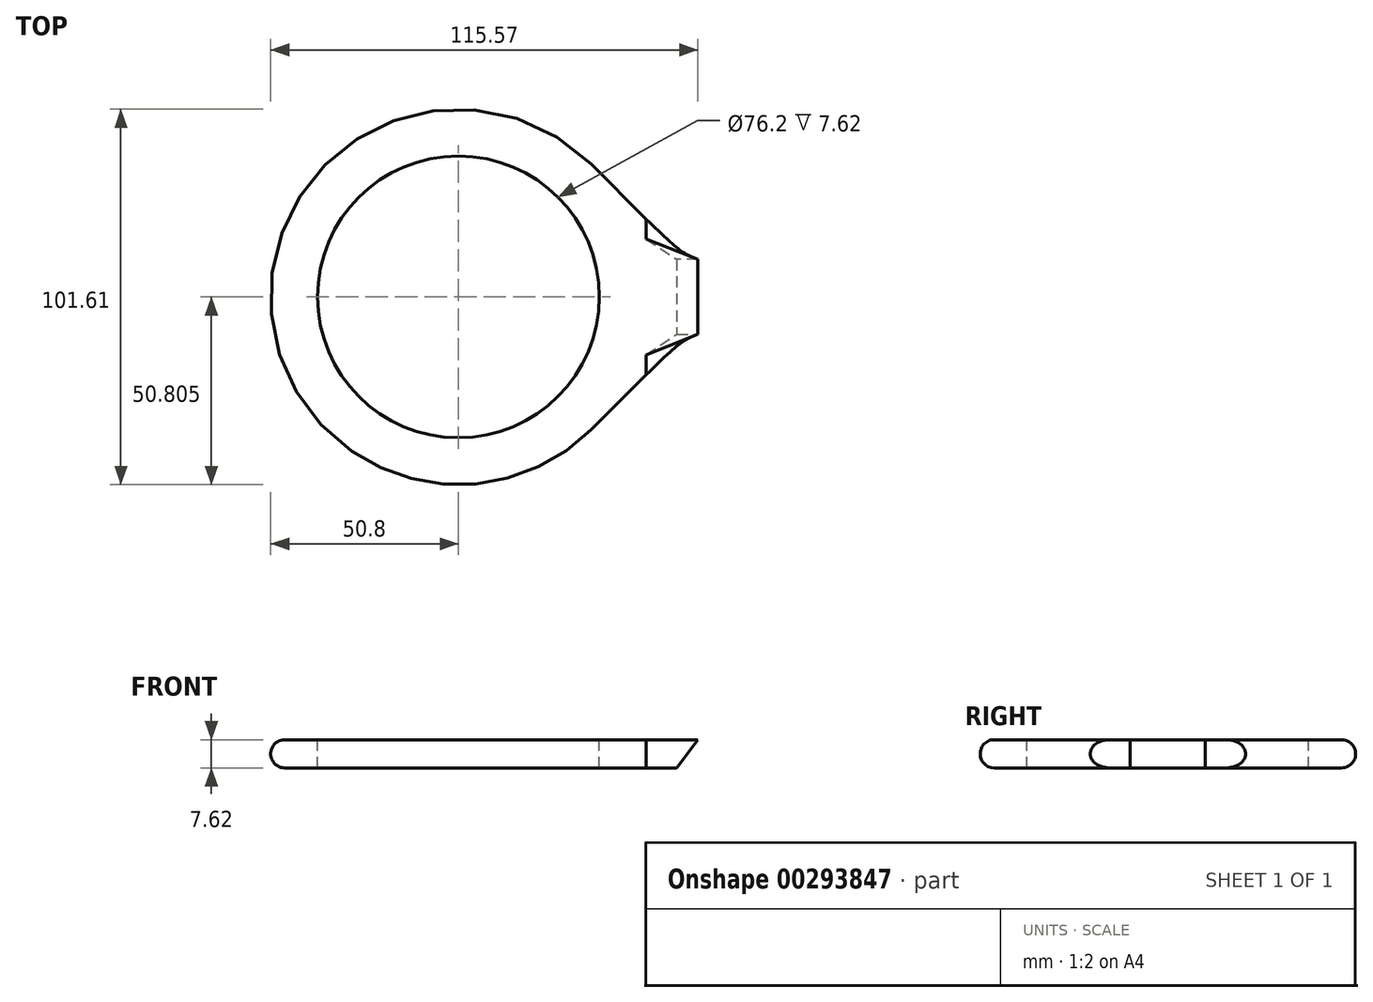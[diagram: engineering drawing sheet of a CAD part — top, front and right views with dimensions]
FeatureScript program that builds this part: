
annotation { "Feature Type Name" : "Feature", "Feature Type Description" : "" }
export const myFeature = defineFeature(function(context is Context, id is Id, definition is map)
    precondition{}
    {
        {
            var Q0;
            Q0=qCreatedBy(makeId("Top.planeOp"),FACE);
            var sketch = newSketch(context, id + "F0", { "sketchPlane" : qUnion([Q0])});
            skLineSegment(sketch, "E0.bottom", {"start": v(31.75, 24.77) * mm, "end": v(-31.75, 24.76) * mm});
            skLineSegment(sketch, "E0.top", {"start": v(31.75, 4.45) * mm, "end": v(-31.75, 4.44) * mm});
            skLineSegment(sketch, "E0.left", {"start": v(31.75, 24.77) * mm, "end": v(31.75, 4.45) * mm});
            skLineSegment(sketch, "E0.right", {"start": v(-31.75, 24.77) * mm, "end": v(-31.75, 4.44) * mm});
            skPoint(sketch, "E0.middle", {"position": v(0, 14.6) * mm});
            skLineSegment(sketch, "E1", {"start": v(-15.88, 24.76) * mm, "end": v(-15.88, 4.44) * mm});
            skLineSegment(sketch, "E2", {"start": v(15.88, 24.77) * mm, "end": v(15.88, 4.44) * mm});
            skCircle(sketch, "E3.cCircle", {"center": v(-82.55, 14.6) * mm, "radius": 50.8 * mm, "construction": true});
            skPoint(sketch, "E3.cCircle.centerSnap0", {"position": v(-31.75, 14.6) * mm});
            skLineSegment(sketch, "E3.0", {"start": v(-31.75, 35.65) * mm, "end": v(-31.75, -6.44) * mm});
            skLineSegment(sketch, "E3.1", {"start": v(-31.75, -6.44) * mm, "end": v(-61.5, -36.2) * mm});
            skLineSegment(sketch, "E3.2", {"start": v(-61.5, -36.2) * mm, "end": v(-103.6, -36.2) * mm});
            skLineSegment(sketch, "E3.3", {"start": v(-103.6, -36.2) * mm, "end": v(-133.35, -6.44) * mm});
            skLineSegment(sketch, "E3.4", {"start": v(-133.35, -6.44) * mm, "end": v(-133.35, 35.65) * mm});
            skLineSegment(sketch, "E3.5", {"start": v(-133.35, 35.65) * mm, "end": v(-103.6, 65.4) * mm});
            skLineSegment(sketch, "E3.6", {"start": v(-103.6, 65.4) * mm, "end": v(-61.5, 65.4) * mm});
            skLineSegment(sketch, "E3.7", {"start": v(-61.5, 65.4) * mm, "end": v(-31.75, 35.65) * mm});
            skPoint(sketch, "E3.0.midPoint", {"position": v(-31.75, 14.6) * mm});
            skCircle(sketch, "E4.cCircle", {"center": v(82.55, 14.6) * mm, "radius": 50.8 * mm, "construction": true});
            skPoint(sketch, "E4.cCircle.centerSnap0", {"position": v(31.75, 14.6) * mm});
            skLineSegment(sketch, "E4.0", {"start": v(31.75, -6.44) * mm, "end": v(31.75, 35.65) * mm});
            skLineSegment(sketch, "E4.1", {"start": v(31.75, 35.65) * mm, "end": v(61.5, 65.4) * mm});
            skLineSegment(sketch, "E4.2", {"start": v(61.5, 65.4) * mm, "end": v(103.6, 65.4) * mm});
            skLineSegment(sketch, "E4.3", {"start": v(103.6, 65.4) * mm, "end": v(133.35, 35.65) * mm});
            skLineSegment(sketch, "E4.4", {"start": v(133.35, 35.65) * mm, "end": v(133.35, -6.44) * mm});
            skLineSegment(sketch, "E4.5", {"start": v(133.35, -6.44) * mm, "end": v(103.6, -36.2) * mm});
            skLineSegment(sketch, "E4.6", {"start": v(103.6, -36.2) * mm, "end": v(61.5, -36.2) * mm});
            skLineSegment(sketch, "E4.7", {"start": v(61.5, -36.2) * mm, "end": v(31.75, -6.44) * mm});
            skPoint(sketch, "E4.0.midPoint", {"position": v(31.75, 14.6) * mm});
            skCircle(sketch, "E5.cCircle", {"center": v(-82.55, 14.6) * mm, "radius": 38.1 * mm, "construction": true});
            skLineSegment(sketch, "E5.0", {"start": v(-98.33, 52.7) * mm, "end": v(-66.77, 52.7) * mm});
            skLineSegment(sketch, "E5.1", {"start": v(-66.77, 52.7) * mm, "end": v(-44.45, 30.39) * mm});
            skLineSegment(sketch, "E5.2", {"start": v(-44.45, 30.39) * mm, "end": v(-44.45, -1.18) * mm});
            skLineSegment(sketch, "E5.3", {"start": v(-44.45, -1.18) * mm, "end": v(-66.77, -23.5) * mm});
            skLineSegment(sketch, "E5.4", {"start": v(-66.77, -23.5) * mm, "end": v(-98.33, -23.5) * mm});
            skLineSegment(sketch, "E5.5", {"start": v(-98.33, -23.5) * mm, "end": v(-120.65, -1.18) * mm});
            skLineSegment(sketch, "E5.6", {"start": v(-120.65, -1.18) * mm, "end": v(-120.65, 30.39) * mm});
            skLineSegment(sketch, "E5.7", {"start": v(-120.65, 30.39) * mm, "end": v(-98.33, 52.7) * mm});
            skPoint(sketch, "E5.0.midPoint", {"position": v(-82.55, 52.7) * mm});
            skCircle(sketch, "E6.cCircle", {"center": v(82.55, 14.6) * mm, "radius": 38.1 * mm, "construction": true});
            skLineSegment(sketch, "E6.0", {"start": v(66.77, 52.7) * mm, "end": v(98.33, 52.7) * mm});
            skLineSegment(sketch, "E6.1", {"start": v(98.33, 52.7) * mm, "end": v(120.65, 30.39) * mm});
            skLineSegment(sketch, "E6.2", {"start": v(120.65, 30.39) * mm, "end": v(120.65, -1.18) * mm});
            skLineSegment(sketch, "E6.3", {"start": v(120.65, -1.18) * mm, "end": v(98.33, -23.5) * mm});
            skLineSegment(sketch, "E6.4", {"start": v(98.33, -23.5) * mm, "end": v(66.77, -23.5) * mm});
            skLineSegment(sketch, "E6.5", {"start": v(66.77, -23.5) * mm, "end": v(44.45, -1.18) * mm});
            skLineSegment(sketch, "E6.6", {"start": v(44.45, -1.18) * mm, "end": v(44.45, 30.39) * mm});
            skLineSegment(sketch, "E6.7", {"start": v(44.45, 30.39) * mm, "end": v(66.77, 52.7) * mm});
            skPoint(sketch, "E6.0.midPoint", {"position": v(82.55, 52.7) * mm});
            skSolve(sketch);
        }
        {
            var Q0;
            {var subQ4=sQuery(id+"F0.wireOp",EDGE,"E3.1");Q0=makeQuery(id+"F0.imprint","IMPRINT",FACE,{"disambiguationData":[TD([[makeQuery(id+"F0.imprint","IMPRINT",EDGE,{"derivedFrom":subQ4}),-1.0]])]});}
            var Q1;
            {var subQ3=sQuery(id+"F0.wireOp",EDGE,"E1");Q1=makeQuery(id+"F0.imprint","IMPRINT",FACE,{"disambiguationData":[TD([[makeQuery(id+"F0.imprint","IMPRINT",EDGE,{"derivedFrom":subQ3}),-1.0]])]});}
            extrude(context, id + "F1", {"entities" : qUnion([Q0, Q1]), "depth" : 7.62 * mm});
        }
        {
            var Q0;
            Q0=makeQuery(id+"F1.opExtrude","CAP_EDGE",EDGE,{"disambiguationData":[OSD([sQuery(id+"F0.wireOp",EDGE,"E1")])],"isStart":true});
            chamfer(context, id + "F2", {"entities" : qUnion([Q0]), "chamferType" : ChamferType.TWO_OFFSETS, "width1" : 7.62 * mm, "oppositeDirection" : false, "width2" : 10.16 * mm, "tangentPropagation" : true});
        }
        {
            var Q0;
            Q0=makeQuery(id+"F1.opExtrude","SWEPT_EDGE",EDGE,{"disambiguationData":[OSD([sQuery(id+"F0.wireOp",EDGE,"E5.0"),sQuery(id+"F0.wireOp",EDGE,"E5.7")])]});
            var Q1;
            Q1=makeQuery(id+"F1.opExtrude","SWEPT_EDGE",EDGE,{"disambiguationData":[OSD([sQuery(id+"F0.wireOp",EDGE,"E5.0"),sQuery(id+"F0.wireOp",EDGE,"E5.1")])]});
            var Q2;
            Q2=makeQuery(id+"F1.opExtrude","SWEPT_EDGE",EDGE,{"disambiguationData":[OSD([sQuery(id+"F0.wireOp",EDGE,"E5.1"),sQuery(id+"F0.wireOp",EDGE,"E5.2")])]});
            var Q3;
            Q3=makeQuery(id+"F1.opExtrude","SWEPT_EDGE",EDGE,{"disambiguationData":[OSD([sQuery(id+"F0.wireOp",EDGE,"E5.2"),sQuery(id+"F0.wireOp",EDGE,"E5.3")])]});
            var Q4;
            Q4=makeQuery(id+"F1.opExtrude","SWEPT_EDGE",EDGE,{"disambiguationData":[OSD([sQuery(id+"F0.wireOp",EDGE,"E5.3"),sQuery(id+"F0.wireOp",EDGE,"E5.4")])]});
            var Q5;
            Q5=makeQuery(id+"F1.opExtrude","SWEPT_EDGE",EDGE,{"disambiguationData":[OSD([sQuery(id+"F0.wireOp",EDGE,"E5.4"),sQuery(id+"F0.wireOp",EDGE,"E5.5")])]});
            var Q6;
            Q6=makeQuery(id+"F1.opExtrude","SWEPT_EDGE",EDGE,{"disambiguationData":[OSD([sQuery(id+"F0.wireOp",EDGE,"E5.5"),sQuery(id+"F0.wireOp",EDGE,"E5.6")])]});
            var Q7;
            Q7=makeQuery(id+"F1.opExtrude","SWEPT_EDGE",EDGE,{"disambiguationData":[OSD([sQuery(id+"F0.wireOp",EDGE,"E5.6"),sQuery(id+"F0.wireOp",EDGE,"E5.7")])]});
            fillet(context, id + "F3", {"entities" : qUnion([Q0, Q1, Q2, Q3, Q4, Q5, Q6, Q7]), "radius" : 38.1 * mm, "tangentPropagation" : true, "allowEdgeOverflow" : false});
        }
        {
            var Q0;
            Q0=makeQuery(id+"F1.opExtrude","SWEPT_EDGE",EDGE,{"disambiguationData":[OSD([sQuery(id+"F0.wireOp",EDGE,"E3.1"),sQuery(id+"F0.wireOp",EDGE,"E3.2")])]});
            var Q1;
            Q1=makeQuery(id+"F1.opExtrude","SWEPT_EDGE",EDGE,{"disambiguationData":[OSD([sQuery(id+"F0.wireOp",EDGE,"E3.2"),sQuery(id+"F0.wireOp",EDGE,"E3.3")])]});
            var Q2;
            Q2=makeQuery(id+"F1.opExtrude","SWEPT_EDGE",EDGE,{"disambiguationData":[OSD([sQuery(id+"F0.wireOp",EDGE,"E3.3"),sQuery(id+"F0.wireOp",EDGE,"E3.4")])]});
            var Q3;
            Q3=makeQuery(id+"F1.opExtrude","SWEPT_EDGE",EDGE,{"disambiguationData":[OSD([sQuery(id+"F0.wireOp",EDGE,"E3.4"),sQuery(id+"F0.wireOp",EDGE,"E3.5")])]});
            var Q4;
            Q4=makeQuery(id+"F1.opExtrude","SWEPT_EDGE",EDGE,{"disambiguationData":[OSD([sQuery(id+"F0.wireOp",EDGE,"E3.5"),sQuery(id+"F0.wireOp",EDGE,"E3.6")])]});
            var Q5;
            Q5=makeQuery(id+"F1.opExtrude","SWEPT_EDGE",EDGE,{"disambiguationData":[OSD([sQuery(id+"F0.wireOp",EDGE,"E3.6"),sQuery(id+"F0.wireOp",EDGE,"E3.7")])]});
            fillet(context, id + "F4", {"entities" : qUnion([Q0, Q1, Q2, Q3, Q4, Q5]), "radius" : 50.8 * mm, "tangentPropagation" : true, "allowEdgeOverflow" : false});
        }
        {
            var Q0;
            {var subQ0=sQuery(id+"F0.wireOp",EDGE,"E3.2");var subQ1=sQuery(id+"F0.wireOp",EDGE,"E3.1");Q0=makeQuery(id+"F4.opFillet","BLEND_EDGE",EDGE,{"blendedFrom":[makeQuery(id+"F1.opExtrude","SWEPT_EDGE",EDGE,{"disambiguationData":[OSD([subQ1,subQ0])]}),makeQuery(id+"F1.opExtrude","CAP_FACE",FACE,{"disambiguationData":[OSD([sQuery(id+"F0.wireOp",EDGE,"E0.bottom"),sQuery(id+"F0.wireOp",EDGE,"E0.top"),sQuery(id+"F0.wireOp",EDGE,"E1"),sQuery(id+"F0.wireOp",EDGE,"E3.0"),subQ1,subQ0,sQuery(id+"F0.wireOp",EDGE,"E3.3"),sQuery(id+"F0.wireOp",EDGE,"E3.4"),sQuery(id+"F0.wireOp",EDGE,"E3.5"),sQuery(id+"F0.wireOp",EDGE,"E3.6"),sQuery(id+"F0.wireOp",EDGE,"E3.7"),sQuery(id+"F0.wireOp",EDGE,"E5.0"),sQuery(id+"F0.wireOp",EDGE,"E5.1"),sQuery(id+"F0.wireOp",EDGE,"E5.2"),sQuery(id+"F0.wireOp",EDGE,"E5.3"),sQuery(id+"F0.wireOp",EDGE,"E5.4"),sQuery(id+"F0.wireOp",EDGE,"E5.5"),sQuery(id+"F0.wireOp",EDGE,"E5.6"),sQuery(id+"F0.wireOp",EDGE,"E5.7")])],"isStart":false})],"blendedInto":[makeQuery(id+"F1.opExtrude","CAP_FACE",FACE,{"disambiguationData":[OSD([sQuery(id+"F0.wireOp",EDGE,"E0.bottom"),sQuery(id+"F0.wireOp",EDGE,"E0.top"),sQuery(id+"F0.wireOp",EDGE,"E1"),sQuery(id+"F0.wireOp",EDGE,"E3.0"),subQ1,subQ0,sQuery(id+"F0.wireOp",EDGE,"E3.3"),sQuery(id+"F0.wireOp",EDGE,"E3.4"),sQuery(id+"F0.wireOp",EDGE,"E3.5"),sQuery(id+"F0.wireOp",EDGE,"E3.6"),sQuery(id+"F0.wireOp",EDGE,"E3.7"),sQuery(id+"F0.wireOp",EDGE,"E5.0"),sQuery(id+"F0.wireOp",EDGE,"E5.1"),sQuery(id+"F0.wireOp",EDGE,"E5.2"),sQuery(id+"F0.wireOp",EDGE,"E5.3"),sQuery(id+"F0.wireOp",EDGE,"E5.4"),sQuery(id+"F0.wireOp",EDGE,"E5.5"),sQuery(id+"F0.wireOp",EDGE,"E5.6"),sQuery(id+"F0.wireOp",EDGE,"E5.7")])],"isStart":false})]});}
            var Q1;
            {var subQ0=sQuery(id+"F0.wireOp",EDGE,"E5.7");var subQ1=sQuery(id+"F0.wireOp",EDGE,"E5.6");var subQ2=sQuery(id+"F0.wireOp",EDGE,"E5.5");var subQ3=sQuery(id+"F0.wireOp",EDGE,"E5.4");var subQ4=sQuery(id+"F0.wireOp",EDGE,"E5.3");var subQ5=sQuery(id+"F0.wireOp",EDGE,"E5.2");var subQ6=sQuery(id+"F0.wireOp",EDGE,"E5.1");var subQ7=sQuery(id+"F0.wireOp",EDGE,"E5.0");var subQ14=sQuery(id+"F0.wireOp",EDGE,"E3.0");var subQ15=sQuery(id+"F0.wireOp",EDGE,"E0.bottom");var subQ16=sQuery(id+"F0.wireOp",EDGE,"E3.7");var subQ19=sQuery(id+"F0.wireOp",EDGE,"E0.top");var subQ20=sQuery(id+"F0.wireOp",EDGE,"E3.6");var subQ21=sQuery(id+"F0.wireOp",EDGE,"E3.5");var subQ22=sQuery(id+"F0.wireOp",EDGE,"E3.4");var subQ23=sQuery(id+"F0.wireOp",EDGE,"E3.3");var subQ24=sQuery(id+"F0.wireOp",EDGE,"E3.2");var subQ25=sQuery(id+"F0.wireOp",EDGE,"E3.1");var subQ26=makeQuery(id+"F1.opExtrude","CAP_FACE",FACE,{"disambiguationData":[OSD([subQ15,subQ19,sQuery(id+"F0.wireOp",EDGE,"E1"),subQ14,subQ25,subQ24,subQ23,subQ22,subQ21,subQ20,subQ16,subQ7,subQ6,subQ5,subQ4,subQ3,subQ2,subQ1,subQ0])],"isStart":true});Q1=makeQuery(id+"F4.opFillet","BLEND_EDGE",EDGE,{"blendedFrom":[makeQuery(id+"F1.opExtrude","SWEPT_EDGE",EDGE,{"disambiguationData":[OSD([subQ25,subQ24])]}),makeQuery(id+"FHjBE7JoIZkxULm_2.boolean.opBoolean","SPLIT",FACE,{"disambiguationData":[TD([makeQuery(id+"F1.opExtrude","SWEPT_FACE",FACE,{"disambiguationData":[OSD([subQ25])]})])],"derivedFrom":subQ26})],"blendedInto":[makeQuery(id+"FHjBE7JoIZkxULm_2.boolean.opBoolean","SPLIT",FACE,{"disambiguationData":[TD([makeQuery(id+"F1.opExtrude","SWEPT_FACE",FACE,{"disambiguationData":[OSD([subQ25])]})])],"derivedFrom":subQ26})]});}
            fillet(context, id + "F5", {"entities" : qUnion([Q0, Q1]), "radius" : 3.8 * mm, "tangentPropagation" : true, "allowEdgeOverflow" : false});
        }
        {
            var Q1;
            {var subQ0=sQuery(id+"F0.wireOp",EDGE,"E3.0");Q1=makeQuery(id+"F1.opExtrude","SWEPT_FACE",FACE,{"disambiguationData":[OSD([subQ0]),TDD([makeQuery(id+"F0.imprint","IMPRINT",EDGE,{"disambiguationData":[TD([[makeQuery(id+"F0.imprint","INTERSECT",VERTEX,{"derivedFrom":[sQuery(id+"F0.wireOp",EDGE,"E0.top"),subQ0]}),-1.0]])],"derivedFrom":subQ0})])]});}
            var Q2;
            Q2=makeQuery(id+"F2.opChamfer","BLEND_FACE",FACE,{"disambiguationData":[OSD([sQuery(id+"F0.wireOp",EDGE,"E1")])]});
            loft(context, id + "F6", {"operationType" : NewBodyOperationType.ADD, "sheetProfilesArray" : [{ "sheetProfileEntities" : qUnion([Q1]) }, { "sheetProfileEntities" : qUnion([Q2]) }]});
        }
        {
            var Q1;
            {var subQ0=sQuery(id+"F0.wireOp",EDGE,"E3.0");Q1=makeQuery(id+"F1.opExtrude","SWEPT_FACE",FACE,{"disambiguationData":[OSD([subQ0]),TDD([makeQuery(id+"F0.imprint","IMPRINT",EDGE,{"disambiguationData":[TD([[makeQuery(id+"F0.imprint","INTERSECT",VERTEX,{"derivedFrom":[sQuery(id+"F0.wireOp",EDGE,"E0.bottom"),subQ0]}),1.0]])],"derivedFrom":subQ0})])]});}
            var Q2;
            Q2=makeQuery(id+"F2.opChamfer","BLEND_FACE",FACE,{"disambiguationData":[OSD([sQuery(id+"F0.wireOp",EDGE,"E1")])]});
            loft(context, id + "F7", {"operationType" : NewBodyOperationType.ADD, "sheetProfilesArray" : [{ "sheetProfileEntities" : qUnion([Q1]) }, { "sheetProfileEntities" : qUnion([Q2]) }]});
        }
    });
